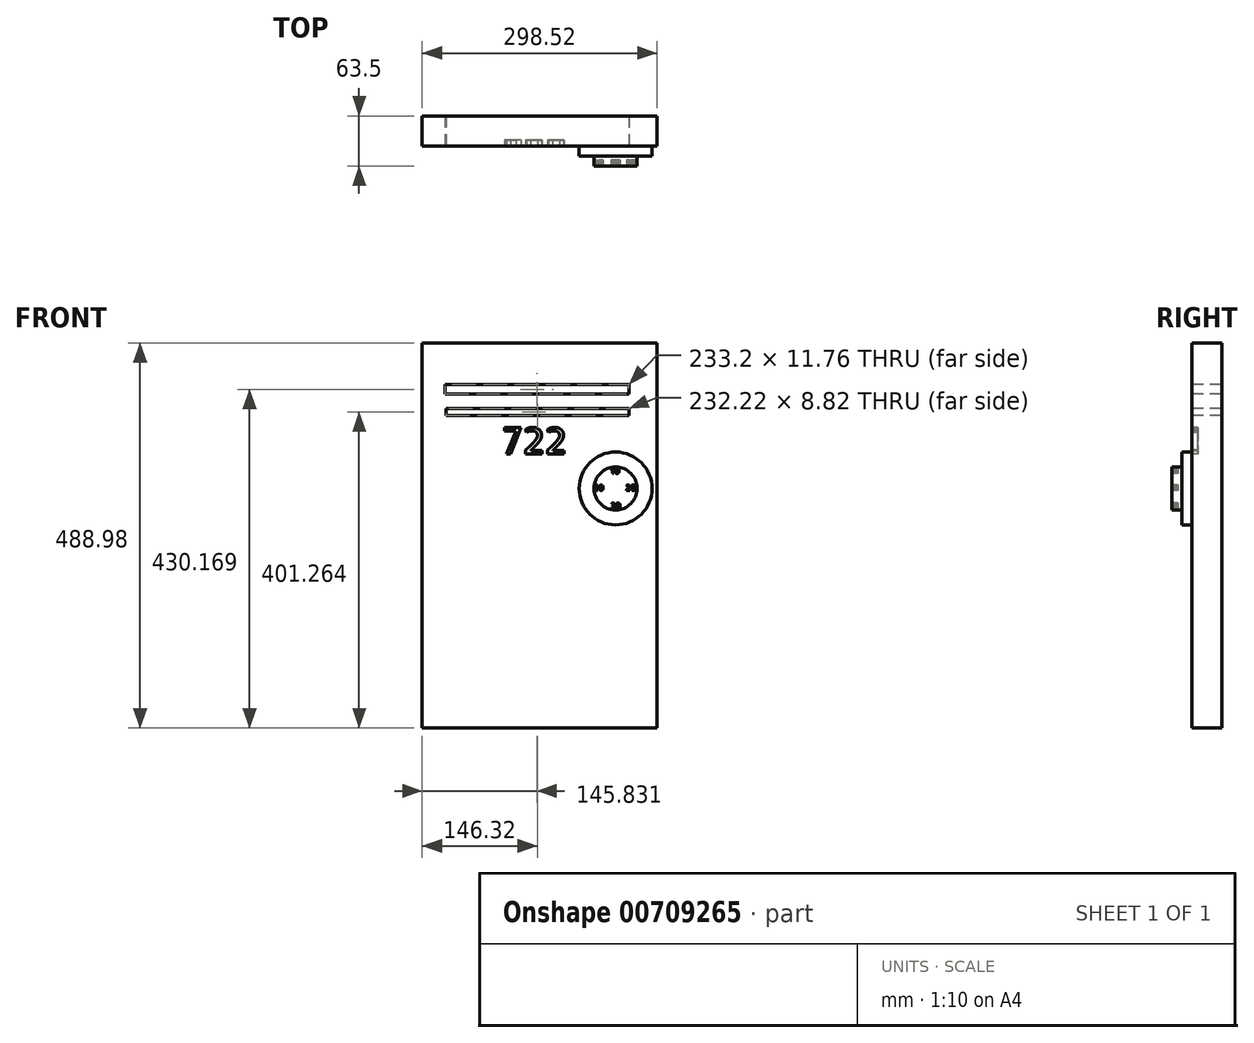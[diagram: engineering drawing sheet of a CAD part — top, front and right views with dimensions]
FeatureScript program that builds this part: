
annotation { "Feature Type Name" : "Feature", "Feature Type Description" : "" }
export const myFeature = defineFeature(function(context is Context, id is Id, definition is map)
    precondition{}
    {
        {
            var Q0;
            Q0=qCreatedBy(makeId("Front.planeOp"),FACE);
            var sketch = newSketch(context, id + "F0", { "sketchPlane" : qUnion([Q0])});
            skLineSegment(sketch, "E0.bottom", {"start": v(-149.26, 244.5) * mm, "end": v(149.26, 244.5) * mm});
            skLineSegment(sketch, "E0.top", {"start": v(-149.26, -244.5) * mm, "end": v(149.26, -244.5) * mm});
            skLineSegment(sketch, "E0.left", {"start": v(-149.26, 244.5) * mm, "end": v(-149.26, -244.5) * mm});
            skLineSegment(sketch, "E0.right", {"start": v(149.26, 244.5) * mm, "end": v(149.26, -244.5) * mm});
            skPoint(sketch, "E0.middle", {"position": v(0, 0) * mm});
            skSolve(sketch);
        }
        {
            var Q0;
            Q0=makeQuery(id+"F0.imprint","IMPRINT",FACE,{"disambiguationData":[TD([[makeQuery(id+"F0.imprint","IMPRINT",EDGE,{"derivedFrom":sQuery(id+"F0.wireOp",EDGE,"E0.bottom")}),-1.0]])]});
            extrude(context, id + "F1", {"entities" : qUnion([Q0]), "depth" : 38.1 * mm, "offsetDistance" : 25.4 * mm});
        }
        {
            var Q0;
            Q0=makeQuery(id+"F1.opExtrude","CAP_FACE",FACE,{"disambiguationData":[OSD([sQuery(id+"F0.wireOp",EDGE,"E0.bottom"),sQuery(id+"F0.wireOp",EDGE,"E0.top"),sQuery(id+"F0.wireOp",EDGE,"E0.left"),sQuery(id+"F0.wireOp",EDGE,"E0.right")])],"isStart":false});
            var sketch = newSketch(context, id + "F2", { "sketchPlane" : qUnion([Q0])});
            skCircle(sketch, "E1", {"center": v(96.4, 59.67) * mm, "radius": 46.28 * mm});
            skSolve(sketch);
        }
        {
            var Q0;
            Q0=makeQuery(id+"F2.imprint","IMPRINT",FACE,{"disambiguationData":[TD([[makeQuery(id+"F2.imprint","IMPRINT",EDGE,{"derivedFrom":sQuery(id+"F2.wireOp",EDGE,"E1")}),1.0]])]});
            extrude(context, id + "F3", {"entities" : qUnion([Q0]), "operationType" : NewBodyOperationType.ADD, "depth" : 12.7 * mm, "offsetDistance" : 25.4 * mm});
        }
        {
            var Q0;
            Q0=makeQuery(id+"F3.opExtrude","CAP_FACE",FACE,{"disambiguationData":[OSD([sQuery(id+"F2.wireOp",EDGE,"E1")])],"isStart":false});
            var sketch = newSketch(context, id + "F4", { "sketchPlane" : qUnion([Q0])});
            skCircle(sketch, "E2", {"center": v(96.4, 59.67) * mm, "radius": 27.29 * mm});
            skSolve(sketch);
        }
        {
            var Q0;
            Q0 = qSketchRegion(id + "F4", true);
            extrude(context, id + "F5", {"entities" : qUnion([Q0]), "operationType" : NewBodyOperationType.ADD, "depth" : 12.7 * mm, "offsetDistance" : 25.4 * mm});
        }
        {
            var Q0;
            Q0=makeQuery(id+"F1.opExtrude","CAP_FACE",FACE,{"disambiguationData":[OSD([sQuery(id+"F0.wireOp",EDGE,"E0.bottom"),sQuery(id+"F0.wireOp",EDGE,"E0.top"),sQuery(id+"F0.wireOp",EDGE,"E0.left"),sQuery(id+"F0.wireOp",EDGE,"E0.right")])],"isStart":false});
            var sketch = newSketch(context, id + "F6", { "sketchPlane" : qUnion([Q0])});
            skSolve(sketch);
        }
        {
            var Q0;
            Q0=makeQuery(id+"F5.opExtrude","CAP_FACE",FACE,{"disambiguationData":[OSD([sQuery(id+"F4.wireOp",EDGE,"E2")])],"isStart":false});
            var sketch = newSketch(context, id + "F7", { "sketchPlane" : qUnion([Q0])});
            skText(sketch, "E3", { "text": "10", "fontName": "AllertaStencil-Regular.ttf"});
            const initialGuessF7  = {"E3": [0.0901, 0.07885, 1, 0, 0.00758]};
            skSetInitialGuess(sketch, initialGuessF7);
            skSolve(sketch);
        }
        {
            var Q0;
            Q0 = qSketchRegion(id + "F7", true);
            extrude(context, id + "F8", {"entities" : qUnion([Q0]), "operationType" : NewBodyOperationType.REMOVE, "oppositeDirection" : true, "depth" : 7.62 * mm, "offsetDistance" : 25.4 * mm});
        }
        {
            var Q0;
            Q0=makeQuery(id+"F5.opExtrude","CAP_FACE",FACE,{"disambiguationData":[OSD([sQuery(id+"F4.wireOp",EDGE,"E2")])],"isStart":false});
            var sketch = newSketch(context, id + "F9", { "sketchPlane" : qUnion([Q0])});
            skText(sketch, "E4", { "text": "20\n", "fontName": "AllertaStencil-Regular.ttf"});
            const initialGuessF9  = {"E4": [0.10962, 0.05723, 1, 0, 0.00687]};
            skSetInitialGuess(sketch, initialGuessF9);
            skSolve(sketch);
        }
        {
            var Q0;
            Q0 = qSketchRegion(id + "F9", true);
            extrude(context, id + "F10", {"entities" : qUnion([Q0]), "operationType" : NewBodyOperationType.REMOVE, "oppositeDirection" : true, "depth" : 7.62 * mm, "offsetDistance" : 25.4 * mm});
        }
        {
            var Q0;
            Q0=makeQuery(id+"F5.opExtrude","CAP_FACE",FACE,{"disambiguationData":[OSD([sQuery(id+"F4.wireOp",EDGE,"E2")])],"isStart":false});
            var sketch = newSketch(context, id + "F11", { "sketchPlane" : qUnion([Q0])});
            skText(sketch, "E5", { "text": "30\n", "fontName": "AllertaStencil-Regular.ttf"});
            const initialGuessF11  = {"E5": [0.09082, 0.03416, 1, 0, 0.00687]};
            skSetInitialGuess(sketch, initialGuessF11);
            skSolve(sketch);
        }
        {
            var Q0;
            Q0 = qSketchRegion(id + "F11", true);
            extrude(context, id + "F12", {"entities" : qUnion([Q0]), "operationType" : NewBodyOperationType.REMOVE, "oppositeDirection" : true, "depth" : 7.62 * mm, "offsetDistance" : 25.4 * mm});
        }
        {
            var Q0;
            Q0=makeQuery(id+"F5.opExtrude","CAP_FACE",FACE,{"disambiguationData":[OSD([sQuery(id+"F4.wireOp",EDGE,"E2")])],"isStart":false});
            var sketch = newSketch(context, id + "F13", { "sketchPlane" : qUnion([Q0])});
            skText(sketch, "E6", { "text": "40\n", "fontName": "AllertaStencil-Regular.ttf"});
            skPoint(sketch, "E6.firstSnap0", {"position": v(112.56, 57.23) * mm});
            const initialGuessF13  = {"E6": [0.06923, 0.05723, 1, 0, 0.0067]};
            skSetInitialGuess(sketch, initialGuessF13);
            skSolve(sketch);
        }
        {
            var Q0;
            Q0 = qSketchRegion(id + "F13", true);
            extrude(context, id + "F14", {"entities" : qUnion([Q0]), "operationType" : NewBodyOperationType.REMOVE, "oppositeDirection" : true, "depth" : 7.62 * mm, "offsetDistance" : 25.4 * mm});
        }
        {
            var Q0;
            Q0=makeQuery(id+"F6.imprint","IMPRINT",FACE,{"disambiguationData":[TD([[makeQuery(id+"F6.imprint","IMPRINT",EDGE,{"derivedFrom":makeQuery(id+"F1.opExtrude","CAP_EDGE",EDGE,{"disambiguationData":[OSD([sQuery(id+"F0.wireOp",EDGE,"E0.bottom")])],"isStart":false})}),-1.0]])]});
            var sketch = newSketch(context, id + "F15", { "sketchPlane" : qUnion([Q0])});
            skLineSegment(sketch, "E7", {"start": v(-120.03, 191.56) * mm, "end": v(113.17, 191.56) * mm});
            skLineSegment(sketch, "E8", {"start": v(113.17, 191.56) * mm, "end": v(113.17, 179.8) * mm});
            skLineSegment(sketch, "E9", {"start": v(113.17, 179.8) * mm, "end": v(-120.03, 179.8) * mm});
            skLineSegment(sketch, "E10", {"start": v(-120.03, 179.8) * mm, "end": v(-120.03, 191.56) * mm});
            skSolve(sketch);
        }
        {
            var Q0;
            Q0 = qSketchRegion(id + "F15", true);
            extrude(context, id + "F16", {"entities" : qUnion([Q0]), "operationType" : NewBodyOperationType.REMOVE, "oppositeDirection" : true, "depth" : 228.6 * mm, "offsetDistance" : 25.4 * mm});
        }
        {
            var Q0;
            Q0=makeQuery(id+"F6.imprint","IMPRINT",FACE,{"disambiguationData":[TD([[makeQuery(id+"F6.imprint","IMPRINT",EDGE,{"derivedFrom":makeQuery(id+"F1.opExtrude","CAP_EDGE",EDGE,{"disambiguationData":[OSD([sQuery(id+"F0.wireOp",EDGE,"E0.bottom")])],"isStart":false})}),-1.0]])]});
            var sketch = newSketch(context, id + "F17", { "sketchPlane" : qUnion([Q0])});
            skLineSegment(sketch, "E11", {"start": v(-119.05, 161.18) * mm, "end": v(113.17, 161.18) * mm});
            skLineSegment(sketch, "E12", {"start": v(113.17, 161.18) * mm, "end": v(113.17, 152.36) * mm});
            skLineSegment(sketch, "E13", {"start": v(-119.05, 161.18) * mm, "end": v(-119.05, 152.36) * mm});
            skLineSegment(sketch, "E14", {"start": v(-119.05, 152.36) * mm, "end": v(113.17, 152.36) * mm});
            skSolve(sketch);
        }
        {
            var Q0;
            Q0 = qSketchRegion(id + "F17", true);
            extrude(context, id + "F18", {"entities" : qUnion([Q0]), "operationType" : NewBodyOperationType.REMOVE, "oppositeDirection" : true, "depth" : 228.6 * mm, "offsetDistance" : 25.4 * mm});
        }
        {
            var Q0;
            Q0=makeQuery(id+"F6.imprint","IMPRINT",FACE,{"disambiguationData":[TD([[makeQuery(id+"F6.imprint","IMPRINT",EDGE,{"derivedFrom":makeQuery(id+"F1.opExtrude","CAP_EDGE",EDGE,{"disambiguationData":[OSD([sQuery(id+"F0.wireOp",EDGE,"E0.bottom")])],"isStart":false})}),-1.0]])]});
            var sketch = newSketch(context, id + "F19", { "sketchPlane" : qUnion([Q0])});
            skText(sketch, "E15", { "text": "722\n", "fontName": "AllertaStencil-Regular.ttf"});
            const initialGuessF19  = {"E15": [-0.04767, 0.10362, 1, 0, 0.03354]};
            skSetInitialGuess(sketch, initialGuessF19);
            skSolve(sketch);
        }
        {
            var Q0;
            Q0 = qSketchRegion(id + "F19", true);
            extrude(context, id + "F20", {"entities" : qUnion([Q0]), "operationType" : NewBodyOperationType.REMOVE, "oppositeDirection" : true, "depth" : 7.62 * mm, "offsetDistance" : 25.4 * mm});
        }
    });
